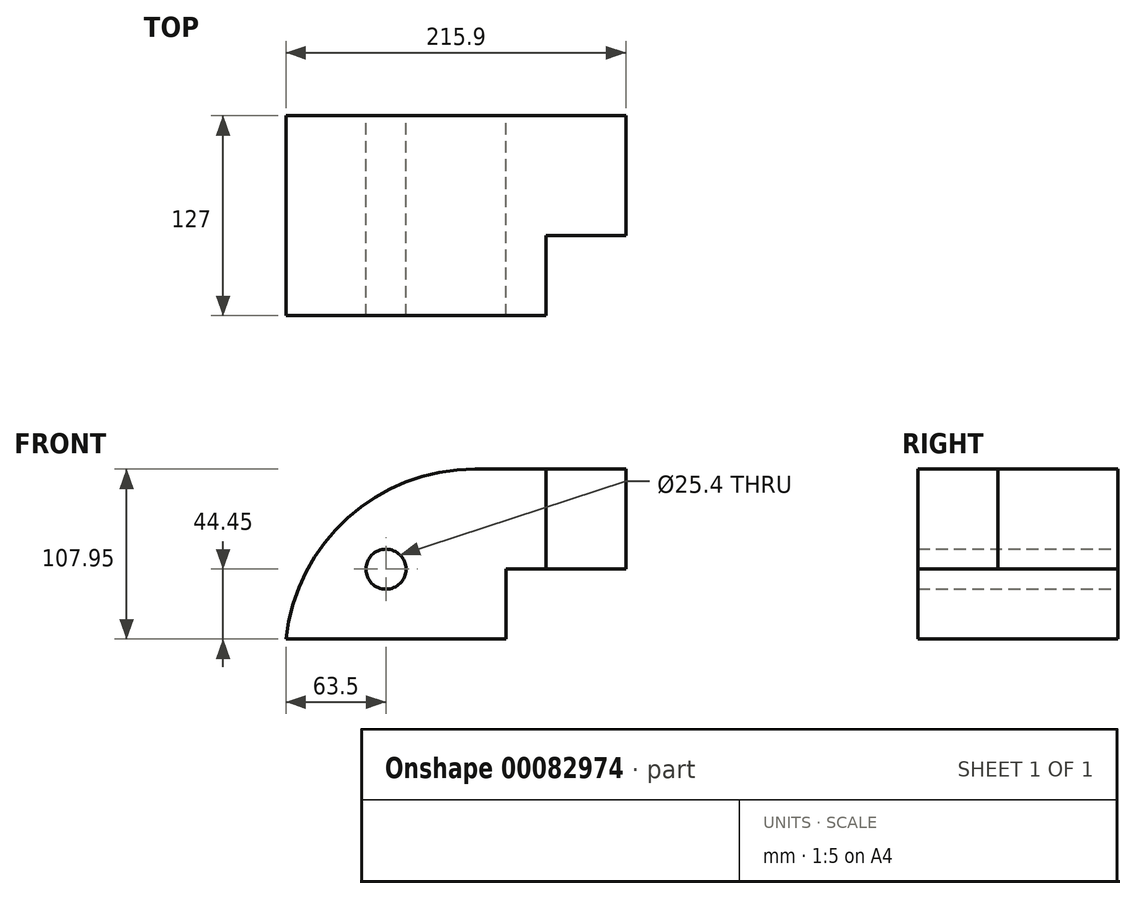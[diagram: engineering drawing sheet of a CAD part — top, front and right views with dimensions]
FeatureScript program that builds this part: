
annotation { "Feature Type Name" : "Feature", "Feature Type Description" : "" }
export const myFeature = defineFeature(function(context is Context, id is Id, definition is map)
    precondition{}
    {
        {
            var Q0;
            Q0=qCreatedBy(makeId("Top.planeOp"),FACE);
            var sketch = newSketch(context, id + "F0", { "sketchPlane" : qUnion([Q0])});
            skLineSegment(sketch, "E0.bottom", {"start": v(121.1, 0) * mm, "end": v(-94.8, 0) * mm});
            skLineSegment(sketch, "E0.top", {"start": v(121.1, 127) * mm, "end": v(-94.8, 127) * mm});
            skLineSegment(sketch, "E0.left", {"start": v(121.1, 0) * mm, "end": v(121.1, 127) * mm});
            skLineSegment(sketch, "E0.right", {"start": v(-94.8, 0) * mm, "end": v(-94.8, 127) * mm});
            skSolve(sketch);
        }
        {
            var Q0;
            Q0=makeQuery(id+"F0.imprint","IMPRINT",FACE,{"disambiguationData":[TD([[makeQuery(id+"F0.imprint","IMPRINT",EDGE,{"derivedFrom":sQuery(id+"F0.wireOp",EDGE,"E0.bottom")}),-1.0]])]});
            extrude(context, id + "F1", {"entities" : qUnion([Q0]), "depth" : 82.55 * mm});
        }
        {
            var Q0;
            Q0=makeQuery(id+"F1.opExtrude","SWEPT_FACE",FACE,{"disambiguationData":[OSD([sQuery(id+"F0.wireOp",EDGE,"E0.top")])]});
            var sketch = newSketch(context, id + "F2", { "sketchPlane" : qUnion([Q0])});
            skLineSegment(sketch, "E1.bottom", {"start": v(-44.9, 0) * mm, "end": v(-121.1, 0) * mm});
            skLineSegment(sketch, "E1.top", {"start": v(-44.9, 44.45) * mm, "end": v(-121.1, 44.45) * mm});
            skLineSegment(sketch, "E1.left", {"start": v(-44.9, 0) * mm, "end": v(-44.9, 44.45) * mm});
            skLineSegment(sketch, "E1.right", {"start": v(-121.1, 0) * mm, "end": v(-121.1, 44.45) * mm});
            skSolve(sketch);
        }
        {
            var Q0;
            Q0 = qSketchRegion(id + "F2", true);
            extrude(context, id + "F3", {"entities" : qUnion([Q0]), "operationType" : NewBodyOperationType.REMOVE, "endBound" : BoundingType.THROUGH_ALL, "oppositeDirection" : true, "depth" : 27.65 * mm});
        }
        {
            var Q0;
            Q0=makeQuery(id+"F1.opExtrude","CAP_FACE",FACE,{"disambiguationData":[OSD([sQuery(id+"F0.wireOp",EDGE,"E0.bottom"),sQuery(id+"F0.wireOp",EDGE,"E0.top"),sQuery(id+"F0.wireOp",EDGE,"E0.left"),sQuery(id+"F0.wireOp",EDGE,"E0.right")])],"isStart":false});
            var sketch = newSketch(context, id + "F4", { "sketchPlane" : qUnion([Q0])});
            skLineSegment(sketch, "E2.bottom", {"start": v(121.1, 37.56) * mm, "end": v(70.3, 37.56) * mm});
            skLineSegment(sketch, "E2.top", {"start": v(121.1, 0) * mm, "end": v(70.3, 0) * mm});
            skLineSegment(sketch, "E2.left", {"start": v(121.1, 37.56) * mm, "end": v(121.1, 0) * mm});
            skLineSegment(sketch, "E2.right", {"start": v(70.3, 37.56) * mm, "end": v(70.3, 0) * mm});
            skSolve(sketch);
        }
        {
            var Q0;
            Q0 = qSketchRegion(id + "F4", true);
            extrude(context, id + "F5", {"entities" : qUnion([Q0]), "operationType" : NewBodyOperationType.REMOVE, "endBound" : BoundingType.THROUGH_ALL, "oppositeDirection" : true, "depth" : 49.72 * mm});
        }
        {
            var Q0;
            Q0=makeQuery(id+"F1.opExtrude","SWEPT_FACE",FACE,{"disambiguationData":[OSD([sQuery(id+"F0.wireOp",EDGE,"E0.left")])]});
            var sketch = newSketch(context, id + "F6", { "sketchPlane" : qUnion([Q0])});
            skCircle(sketch, "E3", {"center": v(84.55, 63.2) * mm, "radius": 7.82 * mm});
            skSolve(sketch);
        }
        {
            var Q0;
            Q0=makeQuery(id+"F6.imprint","IMPRINT",FACE,{"disambiguationData":[TD([[makeQuery(id+"F6.imprint","IMPRINT",EDGE,{"derivedFrom":sQuery(id+"F6.wireOp",EDGE,"E3")}),1.0]])]});
            extrude(context, id + "F7", {"entities" : qUnion([Q0]), "operationType" : NewBodyOperationType.REMOVE, "oppositeDirection" : true, "depth" : 0.25 * mm});
        }
        {
            var Q0;
            Q0=makeQuery(id+"F1.opExtrude","SWEPT_FACE",FACE,{"disambiguationData":[OSD([sQuery(id+"F0.wireOp",EDGE,"E0.top")])]});
            var sketch = newSketch(context, id + "F8", { "sketchPlane" : qUnion([Q0])});
            skCircle(sketch, "E4", {"center": v(31.3, 44.45) * mm, "radius": 12.7 * mm});
            skSolve(sketch);
        }
        {
            var Q0;
            Q0=makeQuery(id+"F8.imprint","IMPRINT",FACE,{"disambiguationData":[TD([[makeQuery(id+"F8.imprint","IMPRINT",EDGE,{"derivedFrom":sQuery(id+"F8.wireOp",EDGE,"E4")}),1.0]])]});
            extrude(context, id + "F9", {"entities" : qUnion([Q0]), "operationType" : NewBodyOperationType.REMOVE, "endBound" : BoundingType.THROUGH_ALL, "oppositeDirection" : true, "depth" : 25.4 * mm});
        }
        {
            var Q0;
            Q0=makeQuery(id+"F1.opExtrude","CAP_EDGE",EDGE,{"disambiguationData":[OSD([sQuery(id+"F0.wireOp",EDGE,"E0.right")])],"isStart":false});
            fillet(context, id + "F10", {"entities" : qUnion([Q0]), "radius" : 120.65 * mm, "tangentPropagation" : true, "allowEdgeOverflow" : false});
        }
        {
            var Q0;
            Q0=makeQuery(id+"F0.imprint","IMPRINT",FACE,{"disambiguationData":[TD([[makeQuery(id+"F0.imprint","IMPRINT",EDGE,{"derivedFrom":sQuery(id+"F0.wireOp",EDGE,"E0.bottom")}),-1.0]])]});
            extrude(context, id + "F11", {"entities" : qUnion([Q0]), "operationType" : NewBodyOperationType.ADD, "depth" : 107.95 * mm});
        }
        {
            var Q0;
            {var subQ0=sQuery(id+"F0.wireOp",EDGE,"E0.left");Q0=makeQuery(id+"F11.boolean.opBoolean","MERGE",FACE,{"derivedFrom":[makeQuery(id+"F1.opExtrude","SWEPT_FACE",FACE,{"disambiguationData":[OSD([subQ0])]}),makeQuery(id+"F11.opExtrude","SWEPT_FACE",FACE,{"disambiguationData":[OSD([subQ0])]})]});}
            var sketch = newSketch(context, id + "F12", { "sketchPlane" : qUnion([Q0])});
            skLineSegment(sketch, "E5.bottom", {"start": v(0, 0) * mm, "end": v(127, 0) * mm});
            skLineSegment(sketch, "E5.top", {"start": v(0, 44.45) * mm, "end": v(127, 44.45) * mm});
            skLineSegment(sketch, "E5.left", {"start": v(0, 0) * mm, "end": v(0, 44.45) * mm});
            skLineSegment(sketch, "E5.right", {"start": v(127, 0) * mm, "end": v(127, 44.45) * mm});
            skLineSegment(sketch, "E6", {"start": v(0, 44.45) * mm, "end": v(0, 107.95) * mm});
            skLineSegment(sketch, "E7.bottom", {"start": v(127, 107.95) * mm, "end": v(50.8, 107.95) * mm});
            skLineSegment(sketch, "E7.top", {"start": v(127, 44.45) * mm, "end": v(50.8, 44.45) * mm});
            skLineSegment(sketch, "E7.left", {"start": v(127, 107.95) * mm, "end": v(127, 44.45) * mm});
            skLineSegment(sketch, "E7.right", {"start": v(50.8, 107.95) * mm, "end": v(50.8, 44.45) * mm});
            skCircle(sketch, "E8", {"center": v(88.9, 76.2) * mm, "radius": 12.7 * mm});
            skSolve(sketch);
        }
        {
            var Q0;
            {var subQ0=sQuery(id+"F12.wireOp",EDGE,"E5.top");Q0=makeQuery(id+"F12.imprint","IMPRINT",FACE,{"disambiguationData":[TD([[makeQuery(id+"F12.imprint","IMPRINT",EDGE,{"derivedFrom":subQ0}),1.0]])]});}
            var sketch = newSketch(context, id + "F13", { "sketchPlane" : qUnion([Q0])});
            skSolve(sketch);
        }
        {
            var Q0;
            {var subQ0=sQuery(id+"F0.wireOp",EDGE,"E0.top");Q0=makeQuery(id+"F11.boolean.opBoolean","MERGE",FACE,{"derivedFrom":[makeQuery(id+"F1.opExtrude","SWEPT_FACE",FACE,{"disambiguationData":[OSD([subQ0])]}),makeQuery(id+"F11.opExtrude","SWEPT_FACE",FACE,{"disambiguationData":[OSD([subQ0])]})]});}
            var sketch = newSketch(context, id + "F14", { "sketchPlane" : qUnion([Q0])});
            skLineSegment(sketch, "E9.bottom", {"start": v(-121.1, 0) * mm, "end": v(-44.9, 0) * mm});
            skLineSegment(sketch, "E9.top", {"start": v(-121.1, 44.45) * mm, "end": v(-44.9, 44.45) * mm});
            skLineSegment(sketch, "E9.left", {"start": v(-121.1, 0) * mm, "end": v(-121.1, 44.45) * mm});
            skLineSegment(sketch, "E9.right", {"start": v(-44.9, 0) * mm, "end": v(-44.9, 44.45) * mm});
            skSolve(sketch);
        }
        {
            var Q0;
            Q0=makeQuery(id+"F14.imprint","IMPRINT",FACE,{"disambiguationData":[TD([[makeQuery(id+"F14.imprint","IMPRINT",EDGE,{"derivedFrom":sQuery(id+"F14.wireOp",EDGE,"E9.bottom")}),1.0]])]});
            extrude(context, id + "F15", {"entities" : qUnion([Q0]), "operationType" : NewBodyOperationType.REMOVE, "endBound" : BoundingType.THROUGH_ALL, "oppositeDirection" : true, "depth" : 25.4 * mm});
        }
        {
            var Q0;
            Q0=makeQuery(id+"F13.imprint","IMPRINT",FACE,{"disambiguationData":[TD([[makeQuery(id+"F13.imprint","IMPRINT",EDGE,{"derivedFrom":makeQuery(id+"F12.imprint","IMPRINT",EDGE,{"derivedFrom":sQuery(id+"F12.wireOp",EDGE,"E5.top")})}),1.0]])]});
            extrude(context, id + "F16", {"entities" : qUnion([Q0]), "operationType" : NewBodyOperationType.REMOVE, "oppositeDirection" : true, "depth" : 50.8 * mm});
        }
        {
            var Q0;
            {var subQ0=sQuery(id+"F0.wireOp",EDGE,"E0.top");Q0=makeQuery(id+"F11.boolean.opBoolean","MERGE",FACE,{"derivedFrom":[makeQuery(id+"F1.opExtrude","SWEPT_FACE",FACE,{"disambiguationData":[OSD([subQ0])]}),makeQuery(id+"F11.opExtrude","SWEPT_FACE",FACE,{"disambiguationData":[OSD([subQ0])]})]});}
            var sketch = newSketch(context, id + "F17", { "sketchPlane" : qUnion([Q0])});
            skCircle(sketch, "E10", {"center": v(31.3, 44.45) * mm, "radius": 12.7 * mm});
            skSolve(sketch);
        }
        {
            var Q0;
            Q0=makeQuery(id+"F17.imprint","IMPRINT",FACE,{"disambiguationData":[TD([[makeQuery(id+"F17.imprint","IMPRINT",EDGE,{"derivedFrom":sQuery(id+"F17.wireOp",EDGE,"E10")}),1.0]])]});
            extrude(context, id + "F18", {"entities" : qUnion([Q0]), "operationType" : NewBodyOperationType.REMOVE, "endBound" : BoundingType.THROUGH_ALL, "oppositeDirection" : true, "depth" : 25.4 * mm});
        }
        {
            var Q0;
            Q0=makeQuery(id+"F11.opExtrude","CAP_EDGE",EDGE,{"disambiguationData":[OSD([sQuery(id+"F0.wireOp",EDGE,"E0.right")])],"isStart":false});
            fillet(context, id + "F19", {"entities" : qUnion([Q0]), "radius" : 120.65 * mm, "tangentPropagation" : true, "allowEdgeOverflow" : false});
        }
    });
